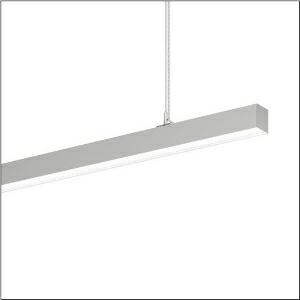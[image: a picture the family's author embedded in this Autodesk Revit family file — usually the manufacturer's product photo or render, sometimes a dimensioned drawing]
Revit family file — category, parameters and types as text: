
# Revit family: silica_21_51mx33tbt9s
name_source: partatom
category: Lighting Fixtures
units: mm (PartAtom-declared; Revit-internal decimal feet)

## family parameters
Cut with Voids When Loaded = No
Host = Face
Light Source = No
Part Type = Normal
Room Calculation Point = No
Round Connector Dimension = Use Diameter
Shared = No

## types (1)
- --- (1 x LED, 7170 lm, 67.4 W, 6500K)
    Apparent Load = 67 VA
    CIE Flux Codes = 78 96 99 56 100
    Color Rendering = 80
    Color Temperature = 6500K
    Default Elevation = 1800 mm
    Description = Silica 21, office luminaire, primary optical cover: prismatic diffuser, of PMMA, CAT 2 (L<= 3000cd/m²), light emission: direct/indirect distribution, primary light characteristic: symmetric, installation type: suspended mounting, LED, rated luminous flux: 7.170lm, luminous efficacy: 101lm/W, light colour: 8tw, colour temperature: 2700..6500K, control gear: DALI DT8, with terminal, 3+2-pole, max. 2.5mm², mains connection: 220..240V, AC, 50/60Hz, rated input power: 70.8W, luminaire housing, of aluminium, metallic grey (RAL 9006), length: 1.504mm, width: 53mm, height: 53mm, protection rating (complete): IP20, insulation class (complete): insulation class I (protective earthing), certification: CE, permissible operating ambient temperature: 0..+35°C, standard: EN 50419, packaging unit: 1 piece
    Height = 53 mm
    Lamp = 1 x LED
    Lamp Light Flux = 7170 lm
    Lamp Power = 67.4 W
    Lamp count = 1
    Length = 1504 mm
    Luminous efficacy = 106 lm/W
    Manufacturer = Siteco
    ModVariant = No
    Model = 51MX33TBT9S
    Mounting Place = Ceiling
    Mounting Type = Pendant
    Number of Poles = 1
    OnlyDefault = Yes
    Power Factor = 1
    Product Name = Silica 21
    Product group = office luminaire | ceiling pendant
    ProductGroupID = 903
    Protection Class = Protection class I
    Protection Degree = IP 20
    RLX_Detail_Level = 1
    RLX_Emergency_Light_Flux = 0 lm
    RLX_Emergency_Type = 0
    RLX_Emergency_Type_DB = No
    RlxData = <blob elided: 20165 chars, md5=e097b3a5>
    Socket = socket
    Standby Power = 0 W
    System Light Flux = 7170 lm
    System Power = 67 W
    Type Comments = individual setting
    Type Image = l_1335864.jpg
    URL = http://relux.com
    VarID = @adj_139235
    Voltage = 0 V
    Weight = 0.00 kg
    Width = 53 mm

## geometry (parser evidence)
native form markers: Blend x4, Sweep x12
no freeform markers — native parametric forms only
